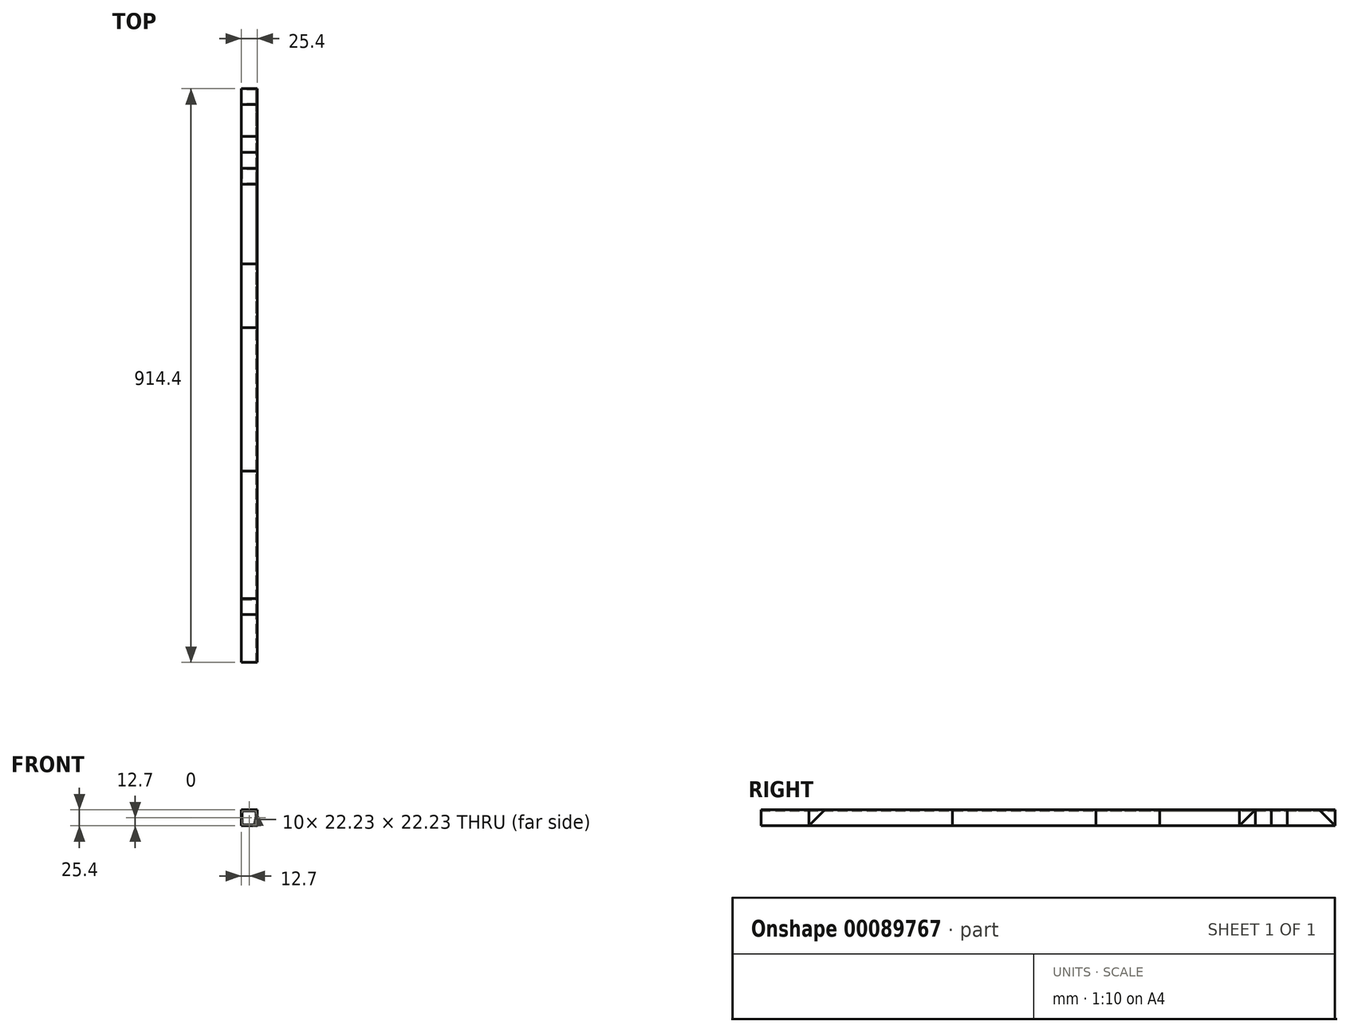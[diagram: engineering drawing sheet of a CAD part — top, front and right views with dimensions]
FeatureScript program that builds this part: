
annotation { "Feature Type Name" : "Feature", "Feature Type Description" : "" }
export const myFeature = defineFeature(function(context is Context, id is Id, definition is map)
    precondition{}
    {
        {
            var Q0;
            Q0=qCreatedBy(makeId("Front.planeOp"),FACE);
            var sketch = newSketch(context, id + "F0", { "sketchPlane" : qUnion([Q0])});
            skLineSegment(sketch, "E0.bottom", {"start": v(0, 0) * mm, "end": v(25.4, 0) * mm});
            skLineSegment(sketch, "E0.top", {"start": v(0, 25.4) * mm, "end": v(25.4, 25.4) * mm});
            skLineSegment(sketch, "E0.left", {"start": v(0, 0) * mm, "end": v(0, 25.4) * mm});
            skLineSegment(sketch, "E0.right", {"start": v(25.4, 0) * mm, "end": v(25.4, 25.4) * mm});
            skLineSegment(sketch, "E1.bottom", {"start": v(1.59, 1.59) * mm, "end": v(23.81, 1.59) * mm});
            skLineSegment(sketch, "E1.top", {"start": v(1.59, 23.81) * mm, "end": v(23.81, 23.81) * mm});
            skLineSegment(sketch, "E1.left", {"start": v(1.59, 1.59) * mm, "end": v(1.59, 23.81) * mm});
            skLineSegment(sketch, "E1.right", {"start": v(23.81, 1.59) * mm, "end": v(23.81, 23.81) * mm});
            skSolve(sketch);
        }
        {
            var Q0;
            Q0=makeQuery(id+"F0.imprint","IMPRINT",FACE,{"disambiguationData":[TD([[makeQuery(id+"F0.imprint","IMPRINT",EDGE,{"derivedFrom":sQuery(id+"F0.wireOp",EDGE,"E0.bottom")}),1.0]])]});
            extrude(context, id + "F1", {"entities" : qUnion([Q0]), "depth" : 914.4 * mm});
        }
        {
            var Q0;
            Q0=qSketchRegion(id+"F0",true);
            extrude(context, id + "F2", {"entities" : qUnion([Q0]), "depth" : 279.4 * mm});
        }
        {
            var Q0;
            Q0=qSketchRegion(id+"F0",true);
            extrude(context, id + "F3", {"entities" : qUnion([Q0]), "depth" : 381 * mm});
        }
        {
            var Q0;
            Q0=qSketchRegion(id+"F0",true);
            extrude(context, id + "F4", {"entities" : qUnion([Q0]), "depth" : 381 * mm});
        }
        {
            var Q0;
            Q0=qSketchRegion(id+"F0",true);
            extrude(context, id + "F5", {"entities" : qUnion([Q0]), "depth" : 609.6 * mm});
        }
        {
            var Q0;
            Q0=qSketchRegion(id+"F0",true);
            extrude(context, id + "F6", {"entities" : qUnion([Q0]), "depth" : 838.2 * mm});
        }
        {
            var Q0;
            Q0=qSketchRegion(id+"F0",true);
            extrude(context, id + "F7", {"entities" : qUnion([Q0]), "depth" : 76.2 * mm});
        }
        {
            var Q0;
            Q0=qSketchRegion(id+"F0",true);
            extrude(context, id + "F8", {"entities" : qUnion([Q0]), "depth" : 838.2 * mm});
        }
        {
            var Q0;
            Q0=qSketchRegion(id+"F0",true);
            extrude(context, id + "F9", {"entities" : qUnion([Q0]), "depth" : 152.4 * mm});
        }
        {
            var Q0;
            Q0=makeQuery(id+"F9.opExtrude","SWEPT_FACE",FACE,{"disambiguationData":[OSD([sQuery(id+"F0.wireOp",EDGE,"E0.right")])]});
            var sketch = newSketch(context, id + "F10", { "sketchPlane" : qUnion([Q0])});
            skLineSegment(sketch, "E2", {"start": v(-152.4, 0) * mm, "end": v(-127, 25.4) * mm});
            skLineSegment(sketch, "E3", {"start": v(0, 0) * mm, "end": v(-25.4, 25.4) * mm});
            skLineSegment(sketch, "E4", {"start": v(-127, 25.4) * mm, "end": v(-152.4, 25.4) * mm});
            skLineSegment(sketch, "E5", {"start": v(-152.4, 0) * mm, "end": v(-152.4, 25.4) * mm});
            skLineSegment(sketch, "E6", {"start": v(-25.4, 25.4) * mm, "end": v(0, 25.4) * mm});
            skSolve(sketch);
        }
        {
            var Q0;
            Q0=makeQuery(id+"F10.imprint","IMPRINT",FACE,{"disambiguationData":[TD([[makeQuery(id+"F10.imprint","IMPRINT",EDGE,{"derivedFrom":sQuery(id+"F10.wireOp",EDGE,"E2")}),1.0]])]});
            var Q1;
            Q1=makeQuery(id+"F10.imprint","IMPRINT",FACE,{"disambiguationData":[TD([[makeQuery(id+"F10.imprint","IMPRINT",EDGE,{"derivedFrom":sQuery(id+"F10.wireOp",EDGE,"E3")}),-1.0]])]});
            extrude(context, id + "F11", {"entities" : qUnion([Q0, Q1]), "operationType" : NewBodyOperationType.REMOVE, "oppositeDirection" : true, "depth" : 25.4 * mm});
        }
        {
            var Q0;
            Q0=makeQuery(id+"F6.opExtrude","SWEPT_FACE",FACE,{"disambiguationData":[OSD([sQuery(id+"F0.wireOp",EDGE,"E0.right")])]});
            var sketch = newSketch(context, id + "F12", { "sketchPlane" : qUnion([Q0])});
            skLineSegment(sketch, "E7", {"start": v(-838.2, 0) * mm, "end": v(-838.2, 25.4) * mm});
            skLineSegment(sketch, "E8", {"start": v(-838.2, 25.4) * mm, "end": v(-812.8, 25.4) * mm});
            skLineSegment(sketch, "E9", {"start": v(-812.8, 25.4) * mm, "end": v(-838.2, 0) * mm});
            skLineSegment(sketch, "E10", {"start": v(0, 0) * mm, "end": v(0, 25.4) * mm});
            skLineSegment(sketch, "E11", {"start": v(0, 25.4) * mm, "end": v(-25.4, 25.4) * mm});
            skLineSegment(sketch, "E12", {"start": v(-25.4, 25.4) * mm, "end": v(0, 0) * mm});
            skSolve(sketch);
        }
        {
            var Q0;
            Q0=makeQuery(id+"F12.imprint","IMPRINT",FACE,{"disambiguationData":[TD([[makeQuery(id+"F12.imprint","IMPRINT",EDGE,{"derivedFrom":sQuery(id+"F12.wireOp",EDGE,"E10")}),1.0]])]});
            var Q1;
            Q1=makeQuery(id+"F12.imprint","IMPRINT",FACE,{"disambiguationData":[TD([[makeQuery(id+"F12.imprint","IMPRINT",EDGE,{"derivedFrom":sQuery(id+"F12.wireOp",EDGE,"E7")}),-1.0]])]});
            extrude(context, id + "F13", {"entities" : qUnion([Q0, Q1]), "operationType" : NewBodyOperationType.REMOVE, "oppositeDirection" : true, "depth" : 25.4 * mm});
        }
        {
            var Q0;
            Q0=qSketchRegion(id+"F0",true);
            extrude(context, id + "F14", {"entities" : qUnion([Q0]), "depth" : 838.2 * mm});
        }
        {
            var Q0;
            Q0=qSketchRegion(id+"F0",true);
            extrude(context, id + "F15", {"entities" : qUnion([Q0]), "depth" : 101.6 * mm});
        }
        {
            var Q0;
            Q0=qSketchRegion(id+"F0",true);
            extrude(context, id + "F16", {"entities" : qUnion([Q0]), "depth" : 127 * mm});
        }
    });
